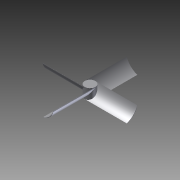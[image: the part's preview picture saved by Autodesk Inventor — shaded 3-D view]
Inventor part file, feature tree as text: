
AUTODESK INVENTOR PART (.ipt)
format: ipt  version: 2012 (Build 160160000, 160)  size: 134,144 bytes
history: native  units: in
note: dims shown in document units (in); Inventor stores cm internally (conversion verified against a paired STEP export)
features: extrude x5, sketch x5, plane x4
ambient origin geometry x8: Origin, YZ Plane, XZ Plane, XY Plane, X Axis, Y Axis, Z Axis, Center Point
bodies: Solid1 (feature_tree)
feature tree (14):
  extrude  "Extrusion1"  Depth=1.0in TaperAngle=0.0deg
  plane  "Work Plane1"
  extrude  "Extrusion2"  Depth=4.0in TaperAngle=0.0deg
  plane  "Work Plane2"
  extrude  "Extrusion3"  Depth=1.29in
  plane  "Work Plane3"
  extrude  "Extrusion4"  [1 undecoded]
  plane  "Work Plane4"
  extrude  "Extrusion5"  Depth=4.0in TaperAngle=0.0deg
  sketch  "Sketch1"  dims[d0=1.0in d1=1.0in d2=0.0in]
  sketch  "Sketch2"  dims[d3=4.0in d4=4.0in d5=0.0in]
  sketch  "Sketch3"  dims[d6=-4.0in d7=1.29in]
  sketch  "Sketch4"  dims[d8=4.0in d9=0.0in d10=-4.0in]
  sketch  "Sketch5"  dims[d11=1.29in d12=4.0in d13=0.0in d14=4.0in d15=4.0in d16=0.0in]
note: 1 required parameter value undecoded (feature->parameter linkage not recoverable at this tier; creation-order binding heuristic only, values carry confidence <= 0.55)
